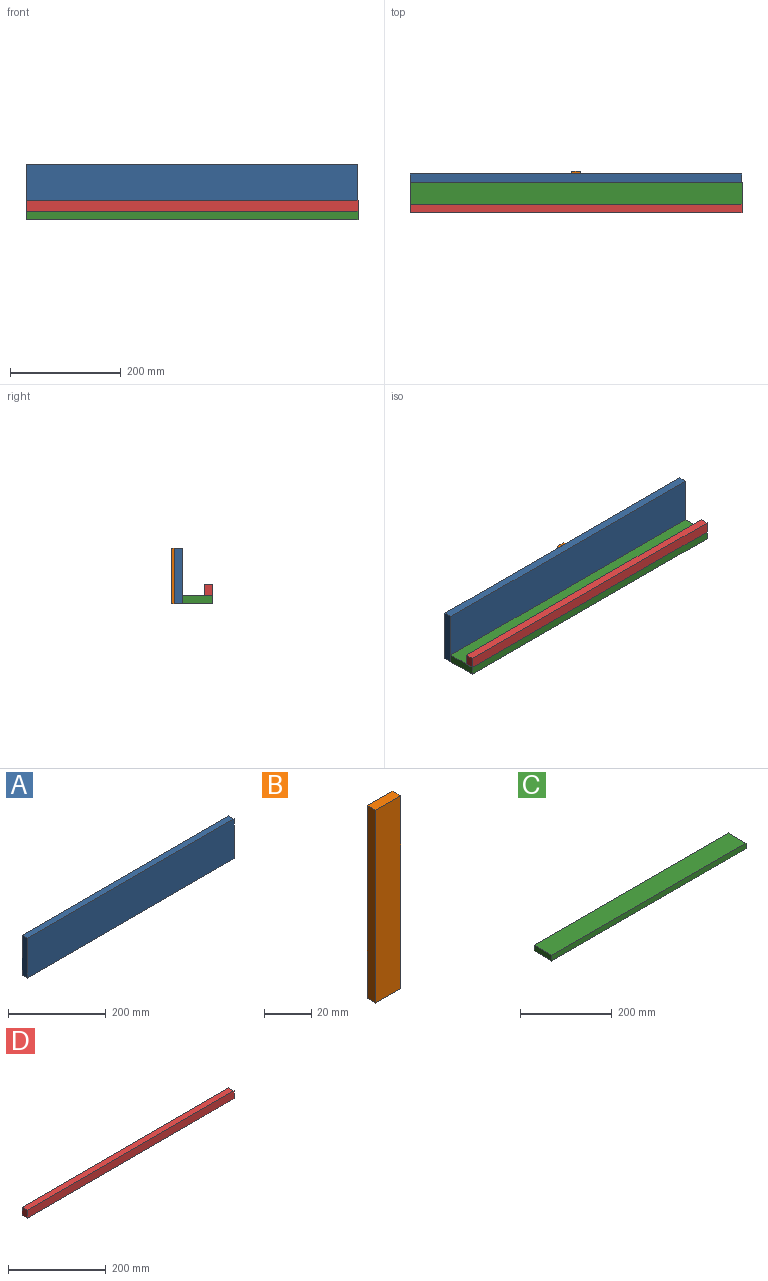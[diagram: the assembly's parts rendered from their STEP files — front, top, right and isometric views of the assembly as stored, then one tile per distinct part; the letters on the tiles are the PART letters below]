
ASSEMBLY  parts=4 mates=3
PART A: 6 faces, bbox 600x15x100 mm
  f0: plane 100x15mm, normal (-1,0,0), area 1500mm2, adj f1,f3,f4,f5
  f1: plane 600x100mm, normal (0,-1,0), area 60000mm2, adj f0,f2,f4,f5
  f2: plane 100x15mm, normal (1,0,0), area 1500mm2, adj f1,f3,f4,f5
  f3: plane 600x100mm, normal (0,1,0), area 60000mm2, adj f0,f2,f4,f5
  f4: plane 600x15mm, normal (0,0,1), area 9000mm2, adj f0,f1,f2,f3
  f5: plane 600x15mm, normal (0,0,-1), area 9000mm2, adj f0,f1,f2,f3
PART B: 6 faces, bbox 15x5x100 mm
  f0: plane 100x5mm, normal (-1,0,0), area 500mm2, adj f1,f3,f4,f5
  f1: plane 15x5mm, normal (0,0,-1), area 75mm2, adj f0,f2,f4,f5
  f2: plane 100x5mm, normal (1,0,0), area 500mm2, adj f1,f3,f4,f5
  f3: plane 15x5mm, normal (0,0,1), area 75mm2, adj f0,f2,f4,f5
  f4: plane 100x15mm, normal (0,-1,0), area 1500mm2, adj f0,f1,f2,f3
  f5: plane 100x15mm, normal (0,1,0), area 1500mm2, adj f0,f1,f2,f3
PART C: 6 faces, bbox 600x55x15 mm
  f0: plane 55x15mm, normal (-1,0,0), area 825mm2, adj f1,f3,f4,f5
  f1: plane 600x55mm, normal (0,0,-1), area 33000mm2, adj f0,f2,f4,f5
  f2: plane 55x15mm, normal (1,0,0), area 825mm2, adj f1,f3,f4,f5
  f3: plane 600x55mm, normal (0,0,1), area 33000mm2, adj f0,f2,f4,f5
  f4: plane 600x15mm, normal (0,-1,0), area 9000mm2, adj f0,f1,f2,f3
  f5: plane 600x15mm, normal (0,1,0), area 9000mm2, adj f0,f1,f2,f3
PART D: 6 faces, bbox 600x15x20 mm
  f0: plane 20x15mm, normal (-1,0,0), area 300mm2, adj f1,f3,f4,f5
  f1: plane 600x20mm, normal (0,-1,0), area 12000mm2, adj f0,f2,f4,f5
  f2: plane 20x15mm, normal (1,0,0), area 300mm2, adj f1,f3,f4,f5
  f3: plane 600x20mm, normal (0,1,0), area 12000mm2, adj f0,f2,f4,f5
  f4: plane 600x15mm, normal (0,0,1), area 9000mm2, adj f0,f1,f2,f3
  f5: plane 600x15mm, normal (0,0,-1), area 9000mm2, adj f0,f1,f2,f3
PLACE A t=(-143.61,97.99,-50.21)mm
PLACE B t=(175.47,117.99,-50.21)mm
PLACE C t=(-117.03,97.99,-50.21)mm
PLACE D t=(-117.03,42.99,-35.21)mm
MATE fastened D.f5 <-> C.f3  axis (0,0,-1) through (482.97,42.99,-35.21)mm
MATE fastened C.f5 <-> A.f1  axis (0,1,0) through (482.97,97.99,-50.21)mm
MATE fastened B.f4 <-> A.f3  axis (0,-1,0) through (182.97,112.99,-0.21)mm
